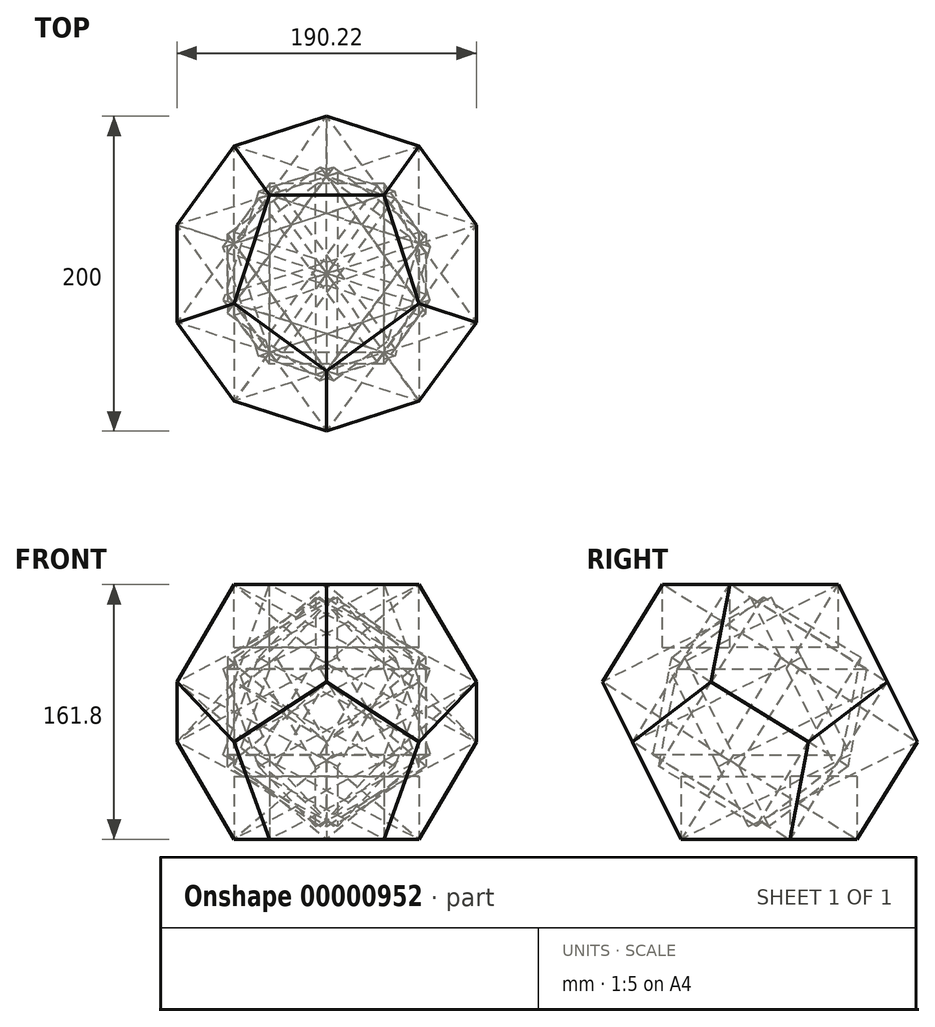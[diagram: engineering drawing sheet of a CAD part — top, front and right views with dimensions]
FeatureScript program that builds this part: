
annotation { "Feature Type Name" : "Feature", "Feature Type Description" : "" }
export const myFeature = defineFeature(function(context is Context, id is Id, definition is map)
    precondition{}
    {
        {
            var Q0;
            Q0=qCreatedBy(makeId("Top.planeOp"),FACE);
            var sketch = newSketch(context, id + "F0", { "sketchPlane" : qUnion([Q0])});
            skCircle(sketch, "E0.cCircle", {"center": v(0, 0) * mm, "radius": 50 * mm, "construction": true});
            skLineSegment(sketch, "E0.0", {"start": v(0, 61.8) * mm, "end": v(58.78, 19.1) * mm});
            skLineSegment(sketch, "E0.1", {"start": v(58.78, 19.1) * mm, "end": v(36.33, -50) * mm});
            skLineSegment(sketch, "E0.2", {"start": v(36.33, -50) * mm, "end": v(-36.33, -50) * mm});
            skLineSegment(sketch, "E0.3", {"start": v(-36.33, -50) * mm, "end": v(-58.78, 19.1) * mm});
            skLineSegment(sketch, "E0.4", {"start": v(-58.78, 19.1) * mm, "end": v(0, 61.8) * mm});
            skPoint(sketch, "E0.0.midPoint", {"position": v(29.39, 40.45) * mm});
            skSolve(sketch);
        }
        {
            var Q0;
            Q0=qCreatedBy(makeId("Right.planeOp"),FACE);
            var sketch = newSketch(context, id + "F1", { "sketchPlane" : qUnion([Q0])});
            skLineSegment(sketch, "E1", {"start": v(-50, 0) * mm, "end": v(-75.48, 50.96) * mm, "construction": true});
            skLineSegment(sketch, "E2", {"start": v(-50, 0) * mm, "end": v(0, 0) * mm, "construction": true});
            skLineSegment(sketch, "E3", {"start": v(0, 0) * mm, "end": v(0, 50.96) * mm, "construction": true});
            skSolve(sketch);
        }
        {
            var Q0;
            Q0=sQuery(id+"F0.wireOp",VERTEX,"E0.1.end");
            var Q1;
            Q1=sQuery(id+"F1.wireOp",VERTEX,"E1.start");
            var Q2;
            Q2=sQuery(id+"F1.wireOp",VERTEX,"E1.end");
            cPlane(context, id + "F2", {"entities" : qUnion([Q0, Q1, Q2]), "cplaneType" : CPlaneType.THREE_POINT, "offset" : 150 * mm, "width" : 150 * mm, "height" : 150 * mm});
        }
        {
            var Q0;
            Q0=qCreatedBy(id+"F2.planeOp",FACE);
            var sketch = newSketch(context, id + "F3", { "sketchPlane" : qUnion([Q0])});
            skCircle(sketch, "E4.cCircle", {"center": v(0, 72.36) * mm, "radius": 50 * mm, "construction": true});
            skLineSegment(sketch, "E4.0", {"start": v(36.33, 22.36) * mm, "end": v(-36.33, 22.36) * mm});
            skLineSegment(sketch, "E4.1", {"start": v(-36.33, 22.36) * mm, "end": v(-58.78, 91.46) * mm});
            skLineSegment(sketch, "E4.2", {"start": v(-58.78, 91.46) * mm, "end": v(0, 134.16) * mm});
            skLineSegment(sketch, "E4.3", {"start": v(0, 134.16) * mm, "end": v(58.78, 91.46) * mm});
            skLineSegment(sketch, "E4.4", {"start": v(58.78, 91.46) * mm, "end": v(36.33, 22.36) * mm});
            skPoint(sketch, "E4.0.midPoint", {"position": v(0, 22.36) * mm});
            skSolve(sketch);
        }
        {
            var Q0;
            Q0=qCreatedBy(makeId("Right.planeOp"),FACE);
            var sketch = newSketch(context, id + "F4", { "sketchPlane" : qUnion([Q0])});
            skLineSegment(sketch, "E5.0", {"start": v(-100, 100) * mm, "end": v(-80.9, 61.8) * mm, "construction": true});
            skLineSegment(sketch, "E6", {"start": v(-90.45, 80.9) * mm, "end": v(61.8, 80.9) * mm, "construction": true});
            skSolve(sketch);
        }
        {
            var Q0;
            Q0=makeQuery(id+"F0.imprint","IMPRINT",FACE,{"disambiguationData":[TD([[makeQuery(id+"F0.imprint","IMPRINT",EDGE,{"derivedFrom":sQuery(id+"F0.wireOp",EDGE,"E0.0")}),-1.0]])]});
            var Q1;
            Q1=qCreatedBy(id+"F2.planeOp",FACE);
            extrude(context, id + "F5", {"entities" : qUnion([Q0]), "endBoundEntity" : qUnion([Q1]), "depth" : 40 * mm});
        }
        {
            var Q0;
            Q0=makeQuery(id+"F3.imprint","IMPRINT",FACE,{"disambiguationData":[TD([[makeQuery(id+"F3.imprint","IMPRINT",EDGE,{"derivedFrom":sQuery(id+"F3.wireOp",EDGE,"E4.0")}),-1.0]])]});
            extrude(context, id + "F6", {"entities" : qUnion([Q0]), "oppositeDirection" : true, "depth" : 120 * mm});
        }
        {
            var Q0;
            Q0=makeQuery(id+"F6.opExtrude","SWEPT_BODY",BODY,{"disambiguationData":[OSD([sQuery(id+"F3.wireOp",EDGE,"E4.0"),sQuery(id+"F3.wireOp",EDGE,"E4.1"),sQuery(id+"F3.wireOp",EDGE,"E4.2"),sQuery(id+"F3.wireOp",EDGE,"E4.3"),sQuery(id+"F3.wireOp",EDGE,"E4.4")])]});
            var Q1;
            Q1=sQuery(id+"F1.wireOp",EDGE,"E3");
            circularPattern(context, id + "F7", {"entities" : qUnion([Q0]), "axis" : qUnion([Q1]), "angle" : 72 * degree, "instanceCount" : 5});
        }
        {
            var Q0;
            Q0=makeQuery(id+"F5.opExtrude","SWEPT_BODY",BODY,{"disambiguationData":[OSD([sQuery(id+"F0.wireOp",EDGE,"E0.0"),sQuery(id+"F0.wireOp",EDGE,"E0.1"),sQuery(id+"F0.wireOp",EDGE,"E0.2"),sQuery(id+"F0.wireOp",EDGE,"E0.3"),sQuery(id+"F0.wireOp",EDGE,"E0.4")])]});
            var Q1;
            Q1=makeQuery(id+"F6.opExtrude","SWEPT_BODY",BODY,{"disambiguationData":[OSD([sQuery(id+"F3.wireOp",EDGE,"E4.0"),sQuery(id+"F3.wireOp",EDGE,"E4.1"),sQuery(id+"F3.wireOp",EDGE,"E4.2"),sQuery(id+"F3.wireOp",EDGE,"E4.3"),sQuery(id+"F3.wireOp",EDGE,"E4.4")])]});
            var Q2;
            Q2=makeQuery(id+"F7.opPattern","COPY",BODY,{"derivedFrom":makeQuery(id+"F6.opExtrude","SWEPT_BODY",BODY,{"disambiguationData":[OSD([sQuery(id+"F3.wireOp",EDGE,"E4.0"),sQuery(id+"F3.wireOp",EDGE,"E4.1"),sQuery(id+"F3.wireOp",EDGE,"E4.2"),sQuery(id+"F3.wireOp",EDGE,"E4.3"),sQuery(id+"F3.wireOp",EDGE,"E4.4")])]}),"instanceName":"1"});
            var Q3;
            Q3=makeQuery(id+"F7.opPattern","COPY",BODY,{"derivedFrom":makeQuery(id+"F6.opExtrude","SWEPT_BODY",BODY,{"disambiguationData":[OSD([sQuery(id+"F3.wireOp",EDGE,"E4.0"),sQuery(id+"F3.wireOp",EDGE,"E4.1"),sQuery(id+"F3.wireOp",EDGE,"E4.2"),sQuery(id+"F3.wireOp",EDGE,"E4.3"),sQuery(id+"F3.wireOp",EDGE,"E4.4")])]}),"instanceName":"2"});
            var Q4;
            Q4=makeQuery(id+"F7.opPattern","COPY",BODY,{"derivedFrom":makeQuery(id+"F6.opExtrude","SWEPT_BODY",BODY,{"disambiguationData":[OSD([sQuery(id+"F3.wireOp",EDGE,"E4.0"),sQuery(id+"F3.wireOp",EDGE,"E4.1"),sQuery(id+"F3.wireOp",EDGE,"E4.2"),sQuery(id+"F3.wireOp",EDGE,"E4.3"),sQuery(id+"F3.wireOp",EDGE,"E4.4")])]}),"instanceName":"3"});
            var Q5;
            Q5=makeQuery(id+"F7.opPattern","COPY",BODY,{"derivedFrom":makeQuery(id+"F6.opExtrude","SWEPT_BODY",BODY,{"disambiguationData":[OSD([sQuery(id+"F3.wireOp",EDGE,"E4.0"),sQuery(id+"F3.wireOp",EDGE,"E4.1"),sQuery(id+"F3.wireOp",EDGE,"E4.2"),sQuery(id+"F3.wireOp",EDGE,"E4.3"),sQuery(id+"F3.wireOp",EDGE,"E4.4")])]}),"instanceName":"4"});
            var Q6;
            Q6=sQuery(id+"F4.wireOp",EDGE,"E6");
            transform(context, id + "F8", {"entities" : qUnion([Q0, Q1, Q2, Q3, Q4, Q5]), "transformType" : TransformType.ROTATION, "transformAxis" : qUnion([Q6]), "angle" : 180 * degree, "oppositeX" : false, "oppositeY" : false, "oppositeZ" : false, "makeCopy" : true});
        }
        {
            var Q0;
            Q0=makeQuery(id+"F8.opPattern","COPY",BODY,{"derivedFrom":makeQuery(id+"F7.opPattern","COPY",BODY,{"derivedFrom":makeQuery(id+"F6.opExtrude","SWEPT_BODY",BODY,{"disambiguationData":[OSD([sQuery(id+"F3.wireOp",EDGE,"E4.0"),sQuery(id+"F3.wireOp",EDGE,"E4.1"),sQuery(id+"F3.wireOp",EDGE,"E4.2"),sQuery(id+"F3.wireOp",EDGE,"E4.3"),sQuery(id+"F3.wireOp",EDGE,"E4.4")])]}),"instanceName":"2"}),"instanceName":"1"});
            var Q1;
            Q1=makeQuery(id+"F8.opPattern","COPY",BODY,{"derivedFrom":makeQuery(id+"F7.opPattern","COPY",BODY,{"derivedFrom":makeQuery(id+"F6.opExtrude","SWEPT_BODY",BODY,{"disambiguationData":[OSD([sQuery(id+"F3.wireOp",EDGE,"E4.0"),sQuery(id+"F3.wireOp",EDGE,"E4.1"),sQuery(id+"F3.wireOp",EDGE,"E4.2"),sQuery(id+"F3.wireOp",EDGE,"E4.3"),sQuery(id+"F3.wireOp",EDGE,"E4.4")])]}),"instanceName":"1"}),"instanceName":"1"});
            var Q2;
            Q2=makeQuery(id+"F8.opPattern","COPY",BODY,{"derivedFrom":makeQuery(id+"F6.opExtrude","SWEPT_BODY",BODY,{"disambiguationData":[OSD([sQuery(id+"F3.wireOp",EDGE,"E4.0"),sQuery(id+"F3.wireOp",EDGE,"E4.1"),sQuery(id+"F3.wireOp",EDGE,"E4.2"),sQuery(id+"F3.wireOp",EDGE,"E4.3"),sQuery(id+"F3.wireOp",EDGE,"E4.4")])]}),"instanceName":"1"});
            var Q3;
            Q3=makeQuery(id+"F8.opPattern","COPY",BODY,{"derivedFrom":makeQuery(id+"F7.opPattern","COPY",BODY,{"derivedFrom":makeQuery(id+"F6.opExtrude","SWEPT_BODY",BODY,{"disambiguationData":[OSD([sQuery(id+"F3.wireOp",EDGE,"E4.0"),sQuery(id+"F3.wireOp",EDGE,"E4.1"),sQuery(id+"F3.wireOp",EDGE,"E4.2"),sQuery(id+"F3.wireOp",EDGE,"E4.3"),sQuery(id+"F3.wireOp",EDGE,"E4.4")])]}),"instanceName":"4"}),"instanceName":"1"});
            var Q4;
            Q4=makeQuery(id+"F8.opPattern","COPY",BODY,{"derivedFrom":makeQuery(id+"F7.opPattern","COPY",BODY,{"derivedFrom":makeQuery(id+"F6.opExtrude","SWEPT_BODY",BODY,{"disambiguationData":[OSD([sQuery(id+"F3.wireOp",EDGE,"E4.0"),sQuery(id+"F3.wireOp",EDGE,"E4.1"),sQuery(id+"F3.wireOp",EDGE,"E4.2"),sQuery(id+"F3.wireOp",EDGE,"E4.3"),sQuery(id+"F3.wireOp",EDGE,"E4.4")])]}),"instanceName":"3"}),"instanceName":"1"});
            var Q5;
            Q5=makeQuery(id+"F8.opPattern","COPY",BODY,{"derivedFrom":makeQuery(id+"F5.opExtrude","SWEPT_BODY",BODY,{"disambiguationData":[OSD([sQuery(id+"F0.wireOp",EDGE,"E0.0"),sQuery(id+"F0.wireOp",EDGE,"E0.1"),sQuery(id+"F0.wireOp",EDGE,"E0.2"),sQuery(id+"F0.wireOp",EDGE,"E0.3"),sQuery(id+"F0.wireOp",EDGE,"E0.4")])]}),"instanceName":"1"});
            var Q6;
            Q6=sQuery(id+"F1.wireOp",EDGE,"E3");
            transform(context, id + "F9", {"entities" : qUnion([Q0, Q1, Q2, Q3, Q4, Q5]), "transformType" : TransformType.ROTATION, "transformAxis" : qUnion([Q6]), "angle" : 36 * degree, "oppositeX" : false, "oppositeY" : false, "oppositeZ" : false, "makeCopy" : false});
        }
    });
